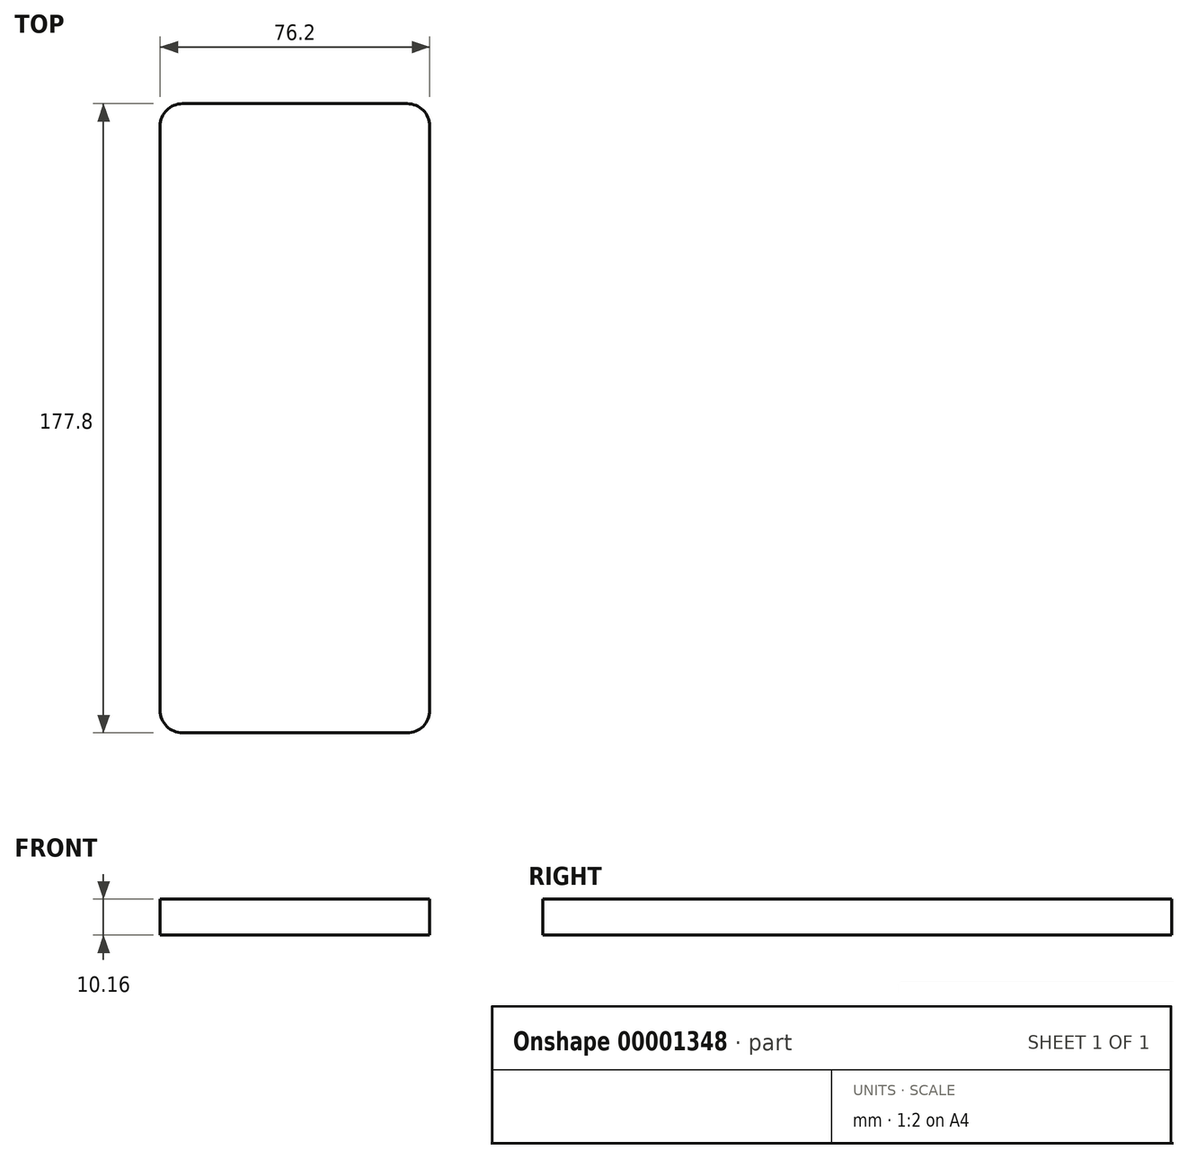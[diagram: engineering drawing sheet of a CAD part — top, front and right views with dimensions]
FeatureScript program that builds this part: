
annotation { "Feature Type Name" : "Feature", "Feature Type Description" : "" }
export const myFeature = defineFeature(function(context is Context, id is Id, definition is map)
    precondition{}
    {
        {
            var Q0;
            Q0=qCreatedBy(makeId("Top.planeOp"),FACE);
            var sketch = newSketch(context, id + "F0", { "sketchPlane" : qUnion([Q0])});
            skLineSegment(sketch, "E0.rect.bottom", {"start": v(31.75, 88.9) * mm, "end": v(-31.75, 88.9) * mm});
            skLineSegment(sketch, "E0.rect.top", {"start": v(31.75, -88.9) * mm, "end": v(-31.75, -88.9) * mm});
            skLineSegment(sketch, "E0.rect.left", {"start": v(38.1, 82.55) * mm, "end": v(38.1, -82.55) * mm});
            skLineSegment(sketch, "E0.rect.right", {"start": v(-38.1, 82.55) * mm, "end": v(-38.1, -82.55) * mm});
            skPoint(sketch, "E0.rect.middle", {"position": v(0, 0) * mm});
            skPoint(sketch, "E1.visualSharp", {"position": v(-38.1, 88.9) * mm});
            skArc(sketch, "E1.filletArc", {"start": v(-31.75, 88.9) * mm, "mid": v(-36.24, 87.04) * mm, "end": v(-38.1, 82.55) * mm});
            skPoint(sketch, "E2.visualSharp", {"position": v(38.1, 88.9) * mm});
            skArc(sketch, "E2.filletArc", {"start": v(38.1, 82.55) * mm, "mid": v(36.24, 87.04) * mm, "end": v(31.75, 88.9) * mm});
            skPoint(sketch, "E3.visualSharp", {"position": v(38.1, -88.9) * mm});
            skArc(sketch, "E3.filletArc", {"start": v(31.75, -88.9) * mm, "mid": v(36.24, -87.04) * mm, "end": v(38.1, -82.55) * mm});
            skPoint(sketch, "E4.visualSharp", {"position": v(-38.1, -88.9) * mm});
            skArc(sketch, "E4.filletArc", {"start": v(-38.1, -82.55) * mm, "mid": v(-36.24, -87.04) * mm, "end": v(-31.75, -88.9) * mm});
            skSolve(sketch);
        }
        {
            var Q0;
            Q0 = qSketchRegion(id + "F0", true);
            extrude(context, id + "F1", {"entities" : qUnion([Q0]), "depth" : 10.16 * mm});
        }
    });
